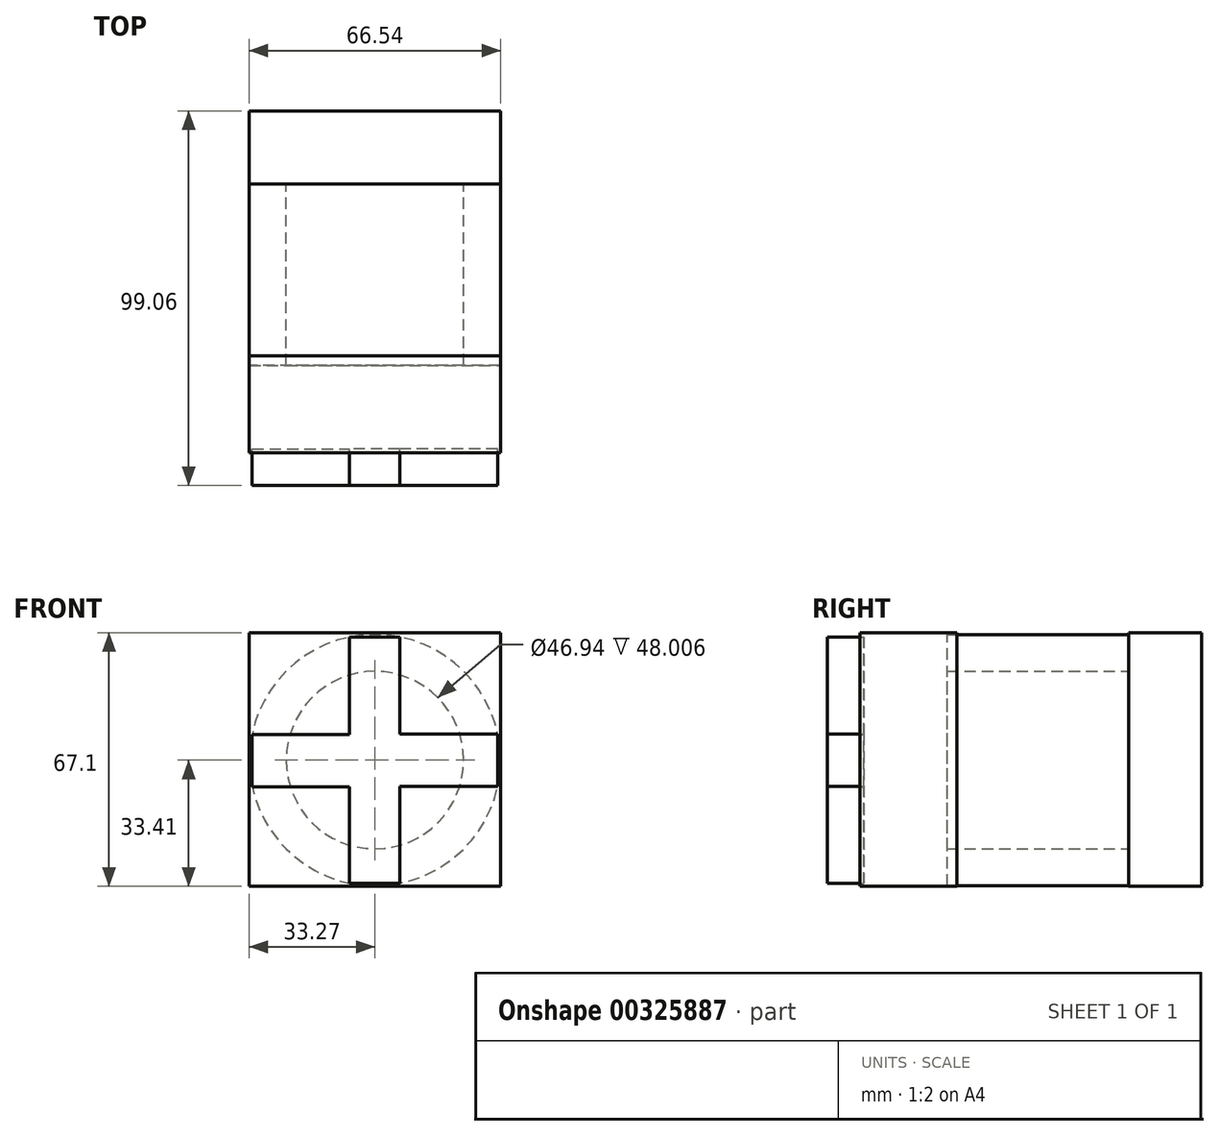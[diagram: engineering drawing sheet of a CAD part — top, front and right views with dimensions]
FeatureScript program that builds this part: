
annotation { "Feature Type Name" : "Feature", "Feature Type Description" : "" }
export const myFeature = defineFeature(function(context is Context, id is Id, definition is map)
    precondition{}
    {
        {
            var Q0;
            Q0=qCreatedBy(makeId("Front.planeOp"),FACE);
            var sketch = newSketch(context, id + "F0", { "sketchPlane" : qUnion([Q0])});
            skCircle(sketch, "E0", {"center": v(0, 0) * mm, "radius": 33.23 * mm});
            skCircle(sketch, "E1", {"center": v(0, 0) * mm, "radius": 23.47 * mm});
            skSolve(sketch);
        }
        {
            var Q0;
            Q0=makeQuery(id+"F0.imprint","IMPRINT",FACE,{"disambiguationData":[TD([[makeQuery(id+"F0.imprint","IMPRINT",EDGE,{"derivedFrom":sQuery(id+"F0.wireOp",EDGE,"E0")}),1.0]])]});
            extrude(context, id + "F1", {"entities" : qUnion([Q0]), "depth" : 48 * mm});
        }
        {
            var Q0;
            Q0=makeQuery(id+"F0.imprint","IMPRINT",FACE,{"disambiguationData":[TD([[makeQuery(id+"F0.imprint","IMPRINT",EDGE,{"derivedFrom":sQuery(id+"F0.wireOp",EDGE,"E0")}),1.0]])]});
            var sketch = newSketch(context, id + "F2", { "sketchPlane" : qUnion([Q0])});
            skLineSegment(sketch, "E2.bottom", {"start": v(-33.27, -33.4) * mm, "end": v(33.27, -33.4) * mm});
            skLineSegment(sketch, "E2.top", {"start": v(-33.27, 33.69) * mm, "end": v(33.27, 33.69) * mm});
            skLineSegment(sketch, "E2.left", {"start": v(-33.27, -33.4) * mm, "end": v(-33.27, 33.69) * mm});
            skLineSegment(sketch, "E2.right", {"start": v(33.27, -33.4) * mm, "end": v(33.27, 33.69) * mm});
            skSolve(sketch);
        }
        {
            var Q0;
            Q0 = qSketchRegion(id + "F2", true);
            extrude(context, id + "F3", {"entities" : qUnion([Q0]), "operationType" : NewBodyOperationType.ADD, "oppositeDirection" : true, "depth" : 19.3 * mm});
        }
        {
            var Q0;
            Q0=makeQuery(id+"F1.opExtrude","CAP_FACE",FACE,{"disambiguationData":[OSD([sQuery(id+"F0.wireOp",EDGE,"E0"),sQuery(id+"F0.wireOp",EDGE,"E1")])],"isStart":false});
            var sketch = newSketch(context, id + "F4", { "sketchPlane" : qUnion([Q0])});
            skLineSegment(sketch, "E3", {"start": v(-6.8, -32.63) * mm, "end": v(-6.8, -7.1) * mm});
            skLineSegment(sketch, "E4", {"start": v(-6.8, -7.1) * mm, "end": v(-32.46, -7.1) * mm});
            skLineSegment(sketch, "E5", {"start": v(-32.46, -7.1) * mm, "end": v(-32.46, 6.8) * mm});
            skLineSegment(sketch, "E6", {"start": v(-32.46, 6.8) * mm, "end": v(-6.8, 6.8) * mm});
            skLineSegment(sketch, "E7", {"start": v(-6.8, 6.8) * mm, "end": v(-6.8, 32.53) * mm});
            skLineSegment(sketch, "E8", {"start": v(-6.8, 32.53) * mm, "end": v(6.55, 32.58) * mm});
            skLineSegment(sketch, "E9", {"start": v(6.55, 32.58) * mm, "end": v(6.55, 6.92) * mm});
            skLineSegment(sketch, "E10", {"start": v(6.55, 6.92) * mm, "end": v(32.5, 6.92) * mm});
            skLineSegment(sketch, "E11", {"start": v(32.5, 6.92) * mm, "end": v(32.5, -6.92) * mm});
            skLineSegment(sketch, "E12", {"start": v(32.5, -6.92) * mm, "end": v(6.55, -6.92) * mm});
            skLineSegment(sketch, "E13", {"start": v(6.55, -6.92) * mm, "end": v(6.55, -32.58) * mm});
            skLineSegment(sketch, "E14", {"start": v(6.55, -32.58) * mm, "end": v(-6.8, -32.63) * mm});
            skSolve(sketch);
        }
        {
            var Q0;
            Q0 = qSketchRegion(id + "F4", true);
            extrude(context, id + "F5", {"entities" : qUnion([Q0]), "depth" : 31.75 * mm, "hasSecondDirection" : true, "secondDirectionOppositeDirection" : false, "secondDirectionDepth" : 22.1 * mm});
        }
        {
            var Q0;
            Q0 = qSketchRegion(id + "F2", true);
            extrude(context, id + "F6", {"entities" : qUnion([Q0]), "depth" : 71.12 * mm, "hasSecondDirection" : true, "secondDirectionOppositeDirection" : false, "secondDirectionDepth" : 45.47 * mm});
        }
    });
